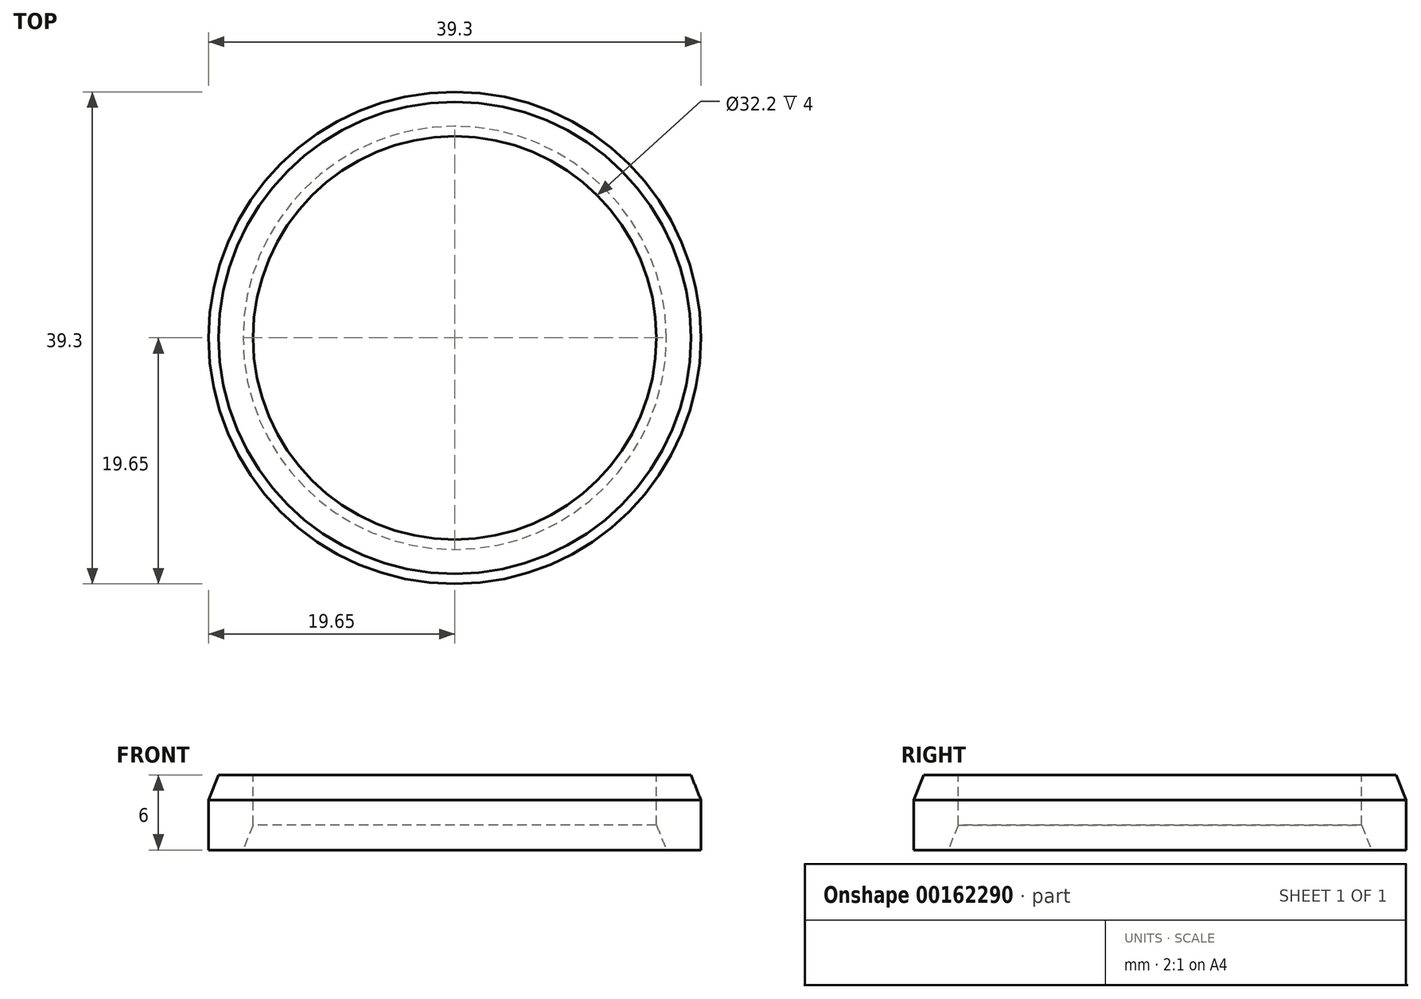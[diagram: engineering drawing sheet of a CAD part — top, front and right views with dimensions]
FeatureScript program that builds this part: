
annotation { "Feature Type Name" : "Feature", "Feature Type Description" : "" }
export const myFeature = defineFeature(function(context is Context, id is Id, definition is map)
    precondition{}
    {
        {
            var Q0;
            Q0=qCreatedBy(makeId("Top.planeOp"),FACE);
            var sketch = newSketch(context, id + "F0", { "sketchPlane" : qUnion([Q0])});
            skCircle(sketch, "E0", {"center": v(0, 0) * mm, "radius": 19.65 * mm});
            skSolve(sketch);
        }
        {
            var Q0;
            Q0 = qSketchRegion(id + "F0", true);
            extrude(context, id + "F1", {"entities" : qUnion([Q0]), "depth" : 6 * mm});
        }
        {
            var Q0;
            Q0=makeQuery(id+"F1.opExtrude","CAP_FACE",FACE,{"disambiguationData":[OSD([sQuery(id+"F0.wireOp",EDGE,"E0")])],"isStart":false});
            var sketch = newSketch(context, id + "F2", { "sketchPlane" : qUnion([Q0])});
            skCircle(sketch, "E1", {"center": v(0, 0) * mm, "radius": 16.1 * mm});
            skSolve(sketch);
        }
        {
            var Q0;
            Q0 = qSketchRegion(id + "F2", true);
            extrude(context, id + "F3", {"entities" : qUnion([Q0]), "operationType" : NewBodyOperationType.REMOVE, "oppositeDirection" : true, "depth" : 25 * mm});
        }
        {
            var Q0;
            Q0=makeQuery(id+"F3.boolean.opBoolean","INTERSECT",EDGE,{"derivedFrom":[makeQuery(id+"F1.opExtrude","CAP_FACE",FACE,{"disambiguationData":[OSD([sQuery(id+"F0.wireOp",EDGE,"E0")])],"isStart":true}),makeQuery(id+"F3.opExtrude","SWEPT_FACE",FACE,{"disambiguationData":[OSD([sQuery(id+"F2.wireOp",EDGE,"E1")])]})]});
            chamfer(context, id + "F4", {"entities" : qUnion([Q0]), "chamferType" : ChamferType.TWO_OFFSETS, "width1" : .8 * mm, "oppositeDirection" : false, "width2" : 2 * mm, "tangentPropagation" : true});
        }
        {
            var Q0;
            Q0=makeQuery(id+"F1.opExtrude","CAP_EDGE",EDGE,{"disambiguationData":[OSD([sQuery(id+"F0.wireOp",EDGE,"E0")])],"isStart":false});
            chamfer(context, id + "F5", {"entities" : qUnion([Q0]), "chamferType" : ChamferType.TWO_OFFSETS, "width1" : .8 * mm, "oppositeDirection" : false, "width2" : 2 * mm, "tangentPropagation" : true});
        }
    });
